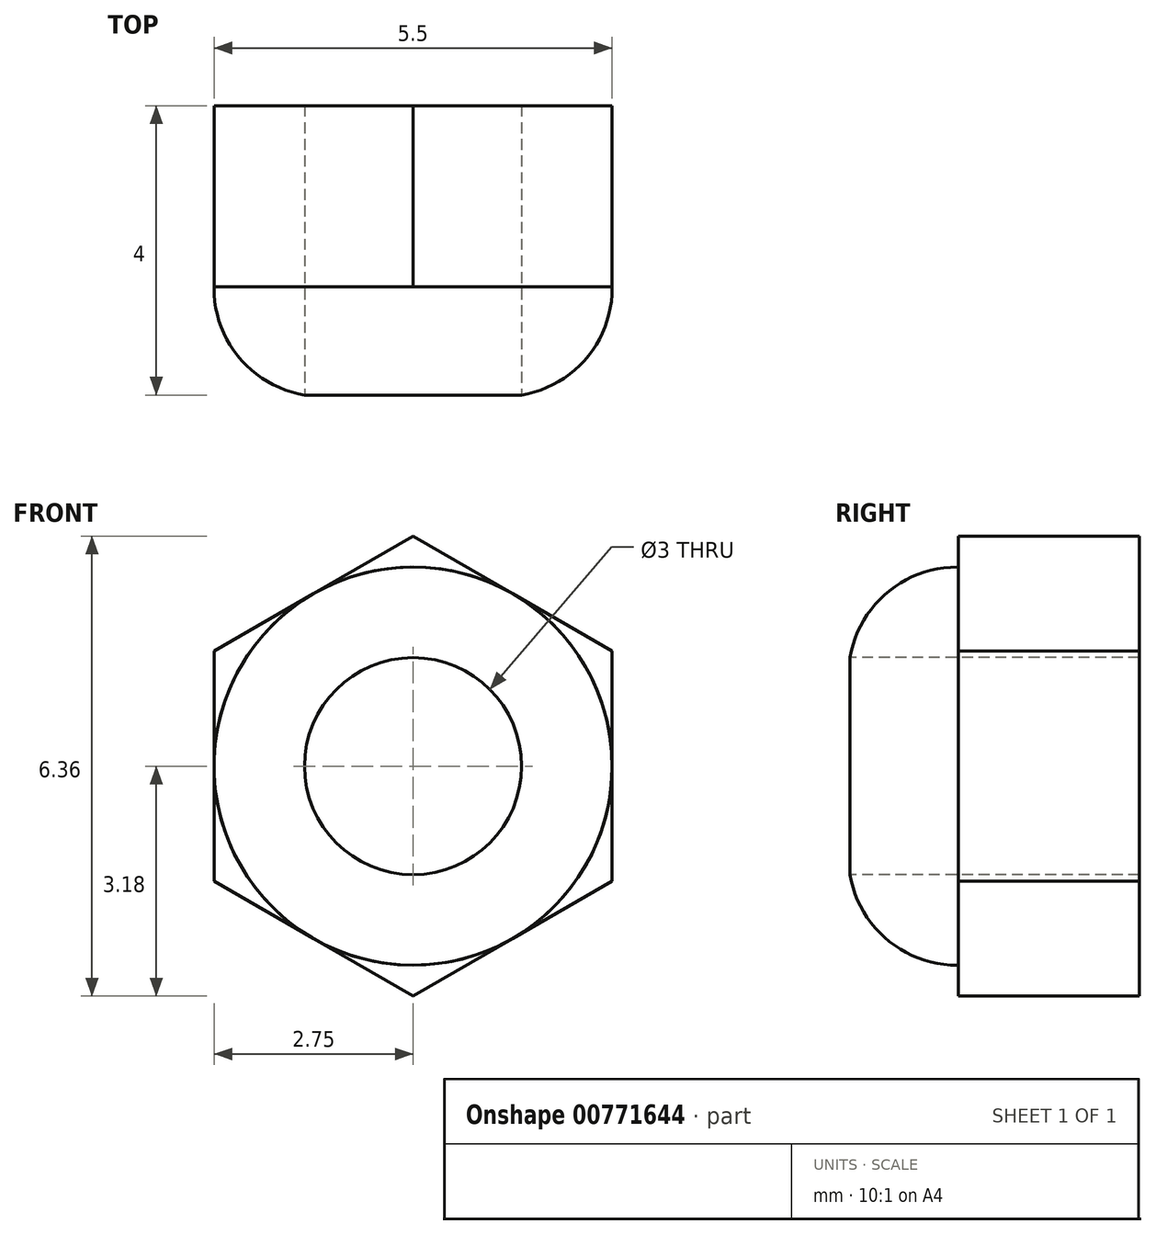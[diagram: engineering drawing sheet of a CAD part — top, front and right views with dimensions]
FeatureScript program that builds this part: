
annotation { "Feature Type Name" : "Feature", "Feature Type Description" : "" }
export const myFeature = defineFeature(function(context is Context, id is Id, definition is map)
    precondition{}
    {
        {
            var Q0;
            Q0=qCreatedBy(makeId("Front.planeOp"),FACE);
            var sketch = newSketch(context, id + "F0", { "sketchPlane" : qUnion([Q0])});
            skCircle(sketch, "E0.cCircle", {"center": v(0, 0) * mm, "radius": 2.75 * mm, "construction": true});
            skLineSegment(sketch, "E0.0", {"start": v(2.75, -1.59) * mm, "end": v(0, -3.18) * mm});
            skLineSegment(sketch, "E0.1", {"start": v(0, -3.18) * mm, "end": v(-2.75, -1.59) * mm});
            skLineSegment(sketch, "E0.2", {"start": v(-2.75, -1.59) * mm, "end": v(-2.75, 1.59) * mm});
            skLineSegment(sketch, "E0.3", {"start": v(-2.75, 1.59) * mm, "end": v(0, 3.18) * mm});
            skLineSegment(sketch, "E0.4", {"start": v(0, 3.18) * mm, "end": v(2.75, 1.59) * mm});
            skLineSegment(sketch, "E0.5", {"start": v(2.75, 1.59) * mm, "end": v(2.75, -1.59) * mm});
            skPoint(sketch, "E0.0.midPoint", {"position": v(1.38, -2.38) * mm});
            skSolve(sketch);
        }
        {
            var Q0;
            Q0 = qSketchRegion(id + "F0", true);
            extrude(context, id + "F1", {"entities" : qUnion([Q0]), "depth" : 2.5 * mm, "offsetDistance" : 25 * mm});
        }
        {
            var Q0;
            Q0=makeQuery(id+"F1.opExtrude","CAP_FACE",FACE,{"disambiguationData":[OSD([sQuery(id+"F0.wireOp",EDGE,"E0.0"),sQuery(id+"F0.wireOp",EDGE,"E0.1"),sQuery(id+"F0.wireOp",EDGE,"E0.2"),sQuery(id+"F0.wireOp",EDGE,"E0.3"),sQuery(id+"F0.wireOp",EDGE,"E0.4"),sQuery(id+"F0.wireOp",EDGE,"E0.5")])],"isStart":false});
            var sketch = newSketch(context, id + "F2", { "sketchPlane" : qUnion([Q0])});
            skCircle(sketch, "E1", {"center": v(0, 0) * mm, "radius": 2.75 * mm});
            skSolve(sketch);
        }
        {
            var Q0;
            Q0 = qSketchRegion(id + "F2", true);
            extrude(context, id + "F3", {"entities" : qUnion([Q0]), "operationType" : NewBodyOperationType.ADD, "depth" : 1.5 * mm, "offsetDistance" : 25 * mm});
        }
        {
            var Q0;
            Q0=makeQuery(id+"F3.opExtrude","CAP_FACE",FACE,{"disambiguationData":[OSD([sQuery(id+"F2.wireOp",EDGE,"E1")])],"isStart":false});
            var sketch = newSketch(context, id + "F4", { "sketchPlane" : qUnion([Q0])});
            skCircle(sketch, "E2", {"center": v(0, 0) * mm, "radius": 1.5 * mm});
            skSolve(sketch);
        }
        {
            var Q0;
            Q0 = qSketchRegion(id + "F4", true);
            extrude(context, id + "F5", {"entities" : qUnion([Q0]), "operationType" : NewBodyOperationType.REMOVE, "endBound" : BoundingType.UP_TO_NEXT, "oppositeDirection" : true, "depth" : 25 * mm, "offsetDistance" : 25 * mm});
        }
        {
            var Q0;
            Q0=makeQuery(id+"F3.opExtrude","CAP_EDGE",EDGE,{"disambiguationData":[OSD([sQuery(id+"F2.wireOp",EDGE,"E1")])],"isStart":false});
            fillet(context, id + "F6", {"entities" : qUnion([Q0]), "radius" : 1.5 * mm, "tangentPropagation" : true, "allowEdgeOverflow" : false});
        }
    });
